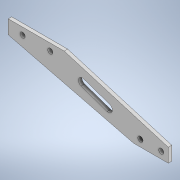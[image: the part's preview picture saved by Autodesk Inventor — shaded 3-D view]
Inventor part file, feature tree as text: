
AUTODESK INVENTOR PART (.ipt)
format: ipt  version: 2020 (Build 240168000, 168)  size: 165,888 bytes
history: native  units: mm
features: other x6, extrude x3, sketch x3, reference x3, projected_geometry x2
ambient origin geometry x8: Origin, YZ Plane, XZ Plane, XY Plane, X Axis, Y Axis, Z Axis, Center Point
bodies: Solid1 (feature_tree)
feature tree (17):
  extrude  "Extrusion1"  Depth=10.0mm
  extrude  "Extrusion3"  Depth=10.0mm
  extrude  "Extrusion4"  Depth=10.0mm
  sketch  "Sketch1"  dims[d0=10.0mm d1=130.0mm]
  reference  "Reference1"
  reference  "Reference2"
  reference  "Reference3"
  sketch  "Sketch3"  dims[d2=32.0mm d3=10.0mm]
  projected_geometry  "Projected Loop2"
  sketch  "Sketch4"  dims[d4=10.0mm d5=20.0mm d6=8.0mm d7=6.0mm d8=3.0mm d9=6.0mm d10=3.0mm d11=2.0mm d12=0.0mm d23=3.0mm d24=3.0mm d25=2.0mm d26=0.0mm d27=8.0mm d28=4.5mm d29=10.0mm d30=0.0mm]
  projected_geometry  "Projected Loop3"
  parser-record x1  (decoder bookkeeping rows leaked as tree rows — omitted from the tree; the rows remain in map.json)
  other  "delta_1.iam"
  other  "arm_holder_1:1"
  other  "arm_1:1"
  other  "arm_shift_1:3"
  other  "pin_8_45:1"
note: 1 file-system path scrubbed to <path> (originals preserved in map.json)
